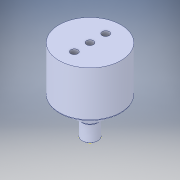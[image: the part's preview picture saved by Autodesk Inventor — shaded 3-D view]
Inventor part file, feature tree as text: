
AUTODESK INVENTOR PART (.ipt)
format: ipt  version: 2018 (Build 220112000, 112)  size: 303,104 bytes
history: native  units: in
note: dims shown in document units (in); Inventor stores cm internally (conversion verified against a paired STEP export)
features: sketch x11, extrude x11, fillet x4, other x4, projected_geometry x3, plane x2, loft x2, pattern_circular x1, chamfer x1
ambient origin geometry x8: Origin, YZ Plane, XZ Plane, XY Plane, X Axis, Y Axis, Z Axis, Center Point
bodies: Solid1 (feature_tree)
feature tree (39):
  plane  "Work Plane1"
  sketch  "Sketch1"  dims[d0=0.3937in d1=0.0in d2=1.75in d3=0.0in]
  extrude  "Extrusion1"  Depth=1.75in TaperAngle=0.0deg
  extrude  "Extrusion2"  Depth=1.0in
  sketch  "Sketch2"  dims[d25=0.45in d26=1.0in]
  extrude  "Extrusion3"  Depth=0.25in
  sketch  "Sketch10"  dims[d35=0.5in d36=0.0in d37=0.0in d38=90.0deg]
  extrude  "Extrusion4"  TaperAngle=0.0deg  [1 undecoded]
  loft  "Loft2"
  loft  "Loft3"
  extrude  "Extrusion5"  Depth=0.481in
  fillet  "Fillet1"  Radius=0.0787in
  extrude  "Extrusion6"  Depth=0.25in TaperAngle=0.0deg
  pattern_circular  "Circular Pattern1"  Count=6  [1 undecoded]
  extrude  "Extrusion7"  Depth=0.25in TaperAngle=0.0deg
  extrude  "Extrusion8"  Depth=1.0in
  fillet  "Fillet2"  Radius=0.25in
  plane  "Work Plane3"
  sketch  "Sketch18"  dims[d61=0.45in d62=1.0in d63=0.25in d64=0.0in]
  extrude  "Extrusion9"  Depth=0.45in
  extrude  "Extrusion10"  Depth=1.0in
  extrude  "Extrusion11"  Depth=0.25in TaperAngle=0.0deg
  chamfer  "Chamfer1"  Distance=0.25in
  fillet  "Fillet3"  Radius=0.25in
  sketch  "Sketch9"  dims[d27=0.625in d28=0.0in d34=0.25in]
  projected_geometry  "Projected Loop7"
  projected_geometry  "Projected Loop8"
  sketch  "Sketch12"  dims[d39=0.0in d40=90.0deg d41=0.0in d42=90.0deg]
  other  "Edges2"
  other  "Edges3"
  other  "Edges4"
  other  "Edges5"
  sketch  "Sketch13"  dims[d43=0.0in d44=90.0deg d45=0.25in d46=0.0in]
  sketch  "Sketch14"  dims[d47=0.125in d49=0.481in d50=0.0787in]
  sketch  "Sketch16"  dims[d51=0.0394in d52=0.25in d53=0.0in d54=2.3622in d55=2.4737in]
  sketch  "Sketch17"  dims[d58=0.0591in d59=0.25in d60=0.0in]
  projected_geometry  "Projected Loop10"
  sketch  "Sketch19"  dims[d65=0.25in d66=0.45in d67=1.0in d68=0.25in d69=0.0in d70=0.25in d71=0.0in d72=0.25in d73=0.0in d74=0.0625in d75=0.0787in d76=45.0deg d77=0.0625in]
  fillet  "Fillet10"  Radius=0.0625in
note: 2 required parameter values undecoded (feature->parameter linkage not recoverable at this tier; creation-order binding heuristic only, values carry confidence <= 0.55)
